# Revit family: Hawkesbury® Top Hung Commercial Sliding Door_XXXXXX
name_source: partatom
category: Doors
units: mm (PartAtom-declared; Revit-internal decimal feet)

## family parameters
Always vertical = Yes
Cut with Voids When Loaded = No
Host = Wall
OmniClass Number = 23.30.20.00
OmniClass Title = Windows
Room Calculation Point = No
Shared = No

## types (1)
- XXX
    Analytic Construction = <None>
    Central Meeting Stiles = 149 mm  [stored 0.488845 ft]
    Date = 21/04/2022
    Define Thermal Properties by = Schematic Type
    Head Offset = 75 mm  [stored 0.246063 ft]
    Height = 0 mm  [stored 0 ft]
    Manufacturer = ALSPEC
    Meeting = 75 mm  [stored 0.246063 ft]
    Model = Hawkesbury® Top Hung Commercial Sliding Door_SG&DG-XXXXXX
    Rough Height = 0 mm  [stored 0 ft]
    Rough Width = 0 mm  [stored 0 ft]
    Sill Offset = 35 mm  [stored 0.114829 ft]
    Thickness = 0 mm  [stored 0 ft]
    URL = https://www.alspec.com.au
    Wall Closure = By host
    Width = 0 mm  [stored 0 ft]

note: [stored X ft] marks values corroborated as IEEE doubles in the binary element streams (Revit-internal decimal feet)

## geometry (parser evidence)
native form markers: Extrusion x4, Sweep x30
no freeform markers — native parametric forms only
